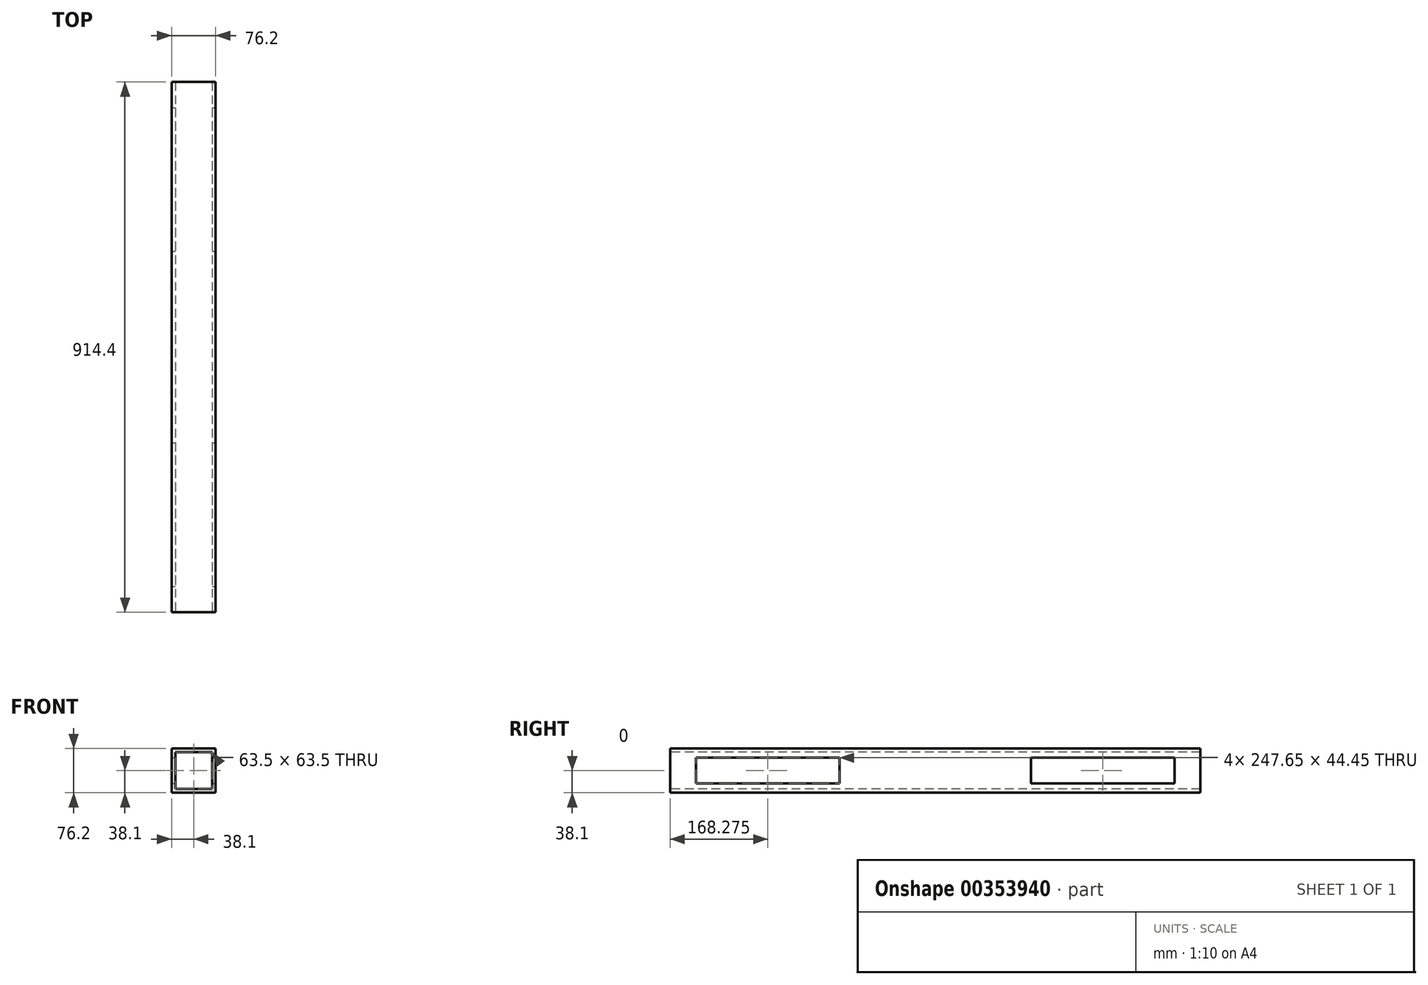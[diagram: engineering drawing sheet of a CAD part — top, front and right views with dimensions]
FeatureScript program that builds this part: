
annotation { "Feature Type Name" : "Feature", "Feature Type Description" : "" }
export const myFeature = defineFeature(function(context is Context, id is Id, definition is map)
    precondition{}
    {
        {
            var Q0;
            Q0=qCreatedBy(makeId("Front.planeOp"),FACE);
            var sketch = newSketch(context, id + "F0", { "sketchPlane" : qUnion([Q0])});
            skLineSegment(sketch, "E0.bottom", {"start": v(31.75, 31.75) * mm, "end": v(-31.75, 31.75) * mm});
            skLineSegment(sketch, "E0.top", {"start": v(31.75, -31.75) * mm, "end": v(-31.75, -31.75) * mm});
            skLineSegment(sketch, "E0.left", {"start": v(31.75, 31.75) * mm, "end": v(31.75, -31.75) * mm});
            skLineSegment(sketch, "E0.right", {"start": v(-31.75, 31.75) * mm, "end": v(-31.75, -31.75) * mm});
            skPoint(sketch, "E0.middle", {"position": v(0, 0) * mm});
            skLineSegment(sketch, "E1.bottom", {"start": v(38.1, -38.1) * mm, "end": v(-38.1, -38.1) * mm});
            skLineSegment(sketch, "E1.top", {"start": v(38.1, 38.1) * mm, "end": v(-38.1, 38.1) * mm});
            skLineSegment(sketch, "E1.left", {"start": v(38.1, -38.1) * mm, "end": v(38.1, 38.1) * mm});
            skLineSegment(sketch, "E1.right", {"start": v(-38.1, -38.1) * mm, "end": v(-38.1, 38.1) * mm});
            skSolve(sketch);
        }
        {
            var Q0;
            Q0 = qSketchRegion(id + "F0", true);
            extrude(context, id + "F1", {"entities" : qUnion([Q0]), "oppositeDirection" : true, "depth" : 914.4 * mm});
        }
        {
            var Q0;
            Q0=makeQuery(id+"F1.opExtrude","SWEPT_FACE",FACE,{"disambiguationData":[OSD([sQuery(id+"F0.wireOp",EDGE,"E1.left")])]});
            var sketch = newSketch(context, id + "F2", { "sketchPlane" : qUnion([Q0])});
            skLineSegment(sketch, "E2.bottom", {"start": v(44.45, 22.22) * mm, "end": v(292.1, 22.23) * mm});
            skLineSegment(sketch, "E2.top", {"start": v(44.45, -22.23) * mm, "end": v(292.1, -22.22) * mm});
            skLineSegment(sketch, "E2.left", {"start": v(44.45, 22.22) * mm, "end": v(44.45, -22.23) * mm});
            skLineSegment(sketch, "E2.right", {"start": v(292.1, 22.23) * mm, "end": v(292.1, -22.22) * mm});
            skLineSegment(sketch, "E3.bottom", {"start": v(622.3, 22.23) * mm, "end": v(869.95, 22.23) * mm});
            skLineSegment(sketch, "E3.top", {"start": v(622.3, -22.23) * mm, "end": v(869.95, -22.22) * mm});
            skLineSegment(sketch, "E3.left", {"start": v(622.3, 22.23) * mm, "end": v(622.3, -22.23) * mm});
            skLineSegment(sketch, "E3.right", {"start": v(869.95, 22.23) * mm, "end": v(869.95, -22.22) * mm});
            skSolve(sketch);
        }
        {
            var Q0;
            Q0 = qSketchRegion(id + "F2", true);
            extrude(context, id + "F3", {"entities" : qUnion([Q0]), "operationType" : NewBodyOperationType.REMOVE, "endBound" : BoundingType.THROUGH_ALL, "oppositeDirection" : true, "depth" : 25.4 * mm});
        }
    });
